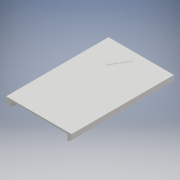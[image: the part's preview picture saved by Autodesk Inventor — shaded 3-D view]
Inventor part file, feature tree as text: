
AUTODESK INVENTOR PART (.ipt)
format: ipt  version: 2017 (Build 210142000, 142)  size: 295,936 bytes
history: native  units: mm
features: projected_geometry x9, sketch x6, other x5, extrude x5, plane x4, shell x1, split x1, mirror x1
ambient origin geometry x8: Origin, YZ Plane, XZ Plane, XY Plane, X Axis, Y Axis, Z Axis, Center Point
bodies: Solid1 (feature_tree)
feature tree (32):
  other  "battery model.ipt"
  shell  "Shell1"  Thickness=10.0mm
  plane  "Work Plane1"
  split  "Split1"
  extrude  "Extrusion1"  [1 undecoded]
  sketch  "Sketch3"  dims[d3=10.0mm d4=0.0mm d5=0.5mm]
  plane  "Work Plane2"
  extrude  "Extrusion2"  Depth=10.0mm
  plane  "Work Plane3"
  extrude  "Extrusion3"  Depth=0.5mm
  extrude  "Extrusion4"  TaperAngle=0.0deg  [1 undecoded]
  extrude  "Extrusion5"  [1 undecoded]
  plane  "Work Plane4"
  mirror  "Mirror1"
  other  "Solid1::battery model.ipt"
  other  "TaggingFeature1"
  sketch  "Sketch1"  dims[d1=1.0mm d2=-2.75mm]
  projected_geometry  "Projected Loop1"
  projected_geometry  "Projected Loop2"
  projected_geometry  "Projected Loop3"
  sketch  "Sketch5"  dims[d8=0.5mm d9=0.0mm]
  projected_geometry  "Projected Loop4"
  projected_geometry  "Projected Loop5"
  sketch  "Sketch4"  dims[d6=0.5mm d7=0.5mm]
  projected_geometry  "Projected Loop6"
  projected_geometry  "Projected Loop7"
  sketch  "Sketch6"  dims[d10=10.0mm d11=0.0mm d12=-0.8mm]
  projected_geometry  "Projected Loop8"
  sketch  "Sketch7"  dims[d13=10.0mm d14=0.0mm d15=1.25mm d16=3.0mm d17=0.0mm d18=0.25mm d19=0.0mm]
  projected_geometry  "Projected Loop9"
  other  "top"
  other  "bottom"
note: 3 required parameter values undecoded (feature->parameter linkage not recoverable at this tier; creation-order binding heuristic only, values carry confidence <= 0.55)
